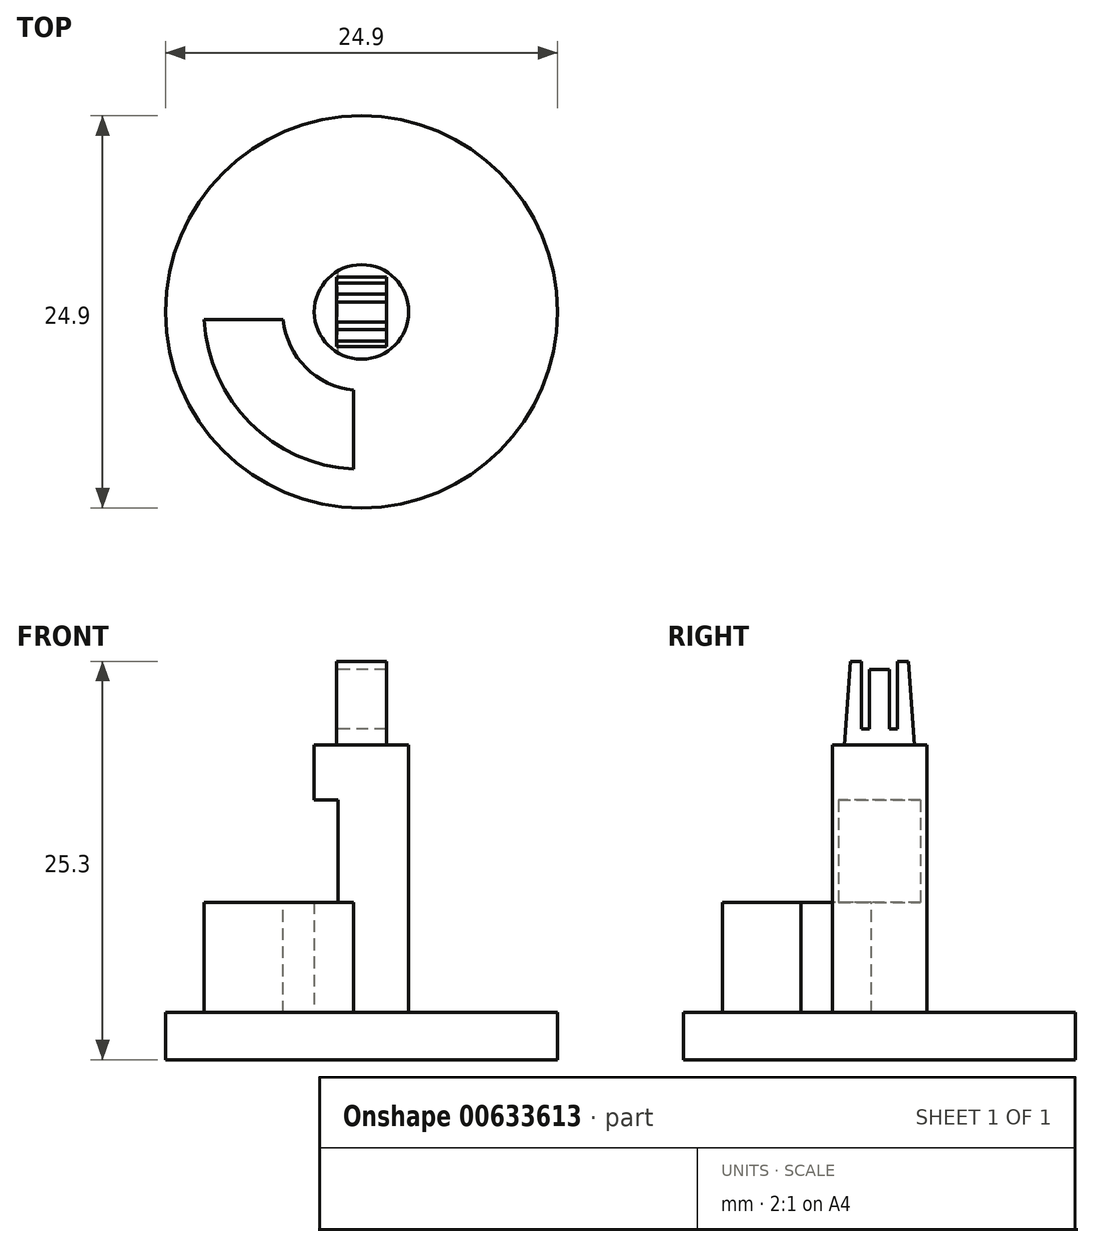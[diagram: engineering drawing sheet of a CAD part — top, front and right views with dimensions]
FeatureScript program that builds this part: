
annotation { "Feature Type Name" : "Feature", "Feature Type Description" : "" }
export const myFeature = defineFeature(function(context is Context, id is Id, definition is map)
    precondition{}
    {
        {
            var Q0;
            Q0=qCreatedBy(makeId("Top.planeOp"),FACE);
            var sketch = newSketch(context, id + "F0", { "sketchPlane" : qUnion([Q0])});
            skCircle(sketch, "E0", {"center": v(0, 0) * mm, "radius": 12.45 * mm});
            skSolve(sketch);
        }
        {
            var Q0;
            Q0=makeQuery(id+"F0.imprint","IMPRINT",FACE,{"disambiguationData":[TD([[makeQuery(id+"F0.imprint","IMPRINT",EDGE,{"derivedFrom":sQuery(id+"F0.wireOp",EDGE,"E0")}),1.0]])]});
            extrude(context, id + "F1", {"entities" : qUnion([Q0]), "depth" : 10 * mm, "offsetDistance" : 25 * mm});
        }
        {
            var Q0;
            Q0=makeQuery(id+"F1.opExtrude","CAP_FACE",FACE,{"disambiguationData":[OSD([sQuery(id+"F0.wireOp",EDGE,"E0")])],"isStart":false});
            var sketch = newSketch(context, id + "F2", { "sketchPlane" : qUnion([Q0])});
            skLineSegment(sketch, "E1", {"start": v(0, 12.45) * mm, "end": v(0, 0) * mm, "construction": true});
            skLineSegment(sketch, "E2", {"start": v(12.45, 0) * mm, "end": v(0, 0) * mm, "construction": true});
            skLineSegment(sketch, "E3", {"start": v(0, -12.45) * mm, "end": v(0, 0) * mm, "construction": true});
            skLineSegment(sketch, "E4", {"start": v(-12.45, 0) * mm, "end": v(0, 0) * mm, "construction": true});
            skCircle(sketch, "E5", {"center": v(0, 0) * mm, "radius": 3 * mm});
            skPoint(sketch, "E6", {"position": v(9.99, 0.5) * mm});
            skPoint(sketch, "E7", {"position": v(0.5, 9.99) * mm});
            skPoint(sketch, "E8", {"position": v(0.5, 4.97) * mm});
            skPoint(sketch, "E9", {"position": v(4.97, 0.5) * mm});
            skArc(sketch, "E10", {"start": v(9.99, 0.5) * mm, "mid": v(7.07, 7.07) * mm, "end": v(0.5, 9.99) * mm});
            skArc(sketch, "E11", {"start": v(0.5, 4.97) * mm, "mid": v(3.54, 3.54) * mm, "end": v(4.97, 0.5) * mm});
            skLineSegment(sketch, "E12", {"start": v(0.5, 9.99) * mm, "end": v(0.5, 4.97) * mm});
            skLineSegment(sketch, "E13", {"start": v(9.99, 0.5) * mm, "end": v(4.97, 0.5) * mm});
            skLineSegment(sketch, "E14.MirrorCS", {"start": v(9.99, -0.5) * mm, "end": v(4.97, -0.5) * mm});
            skArc(sketch, "E15.MirrorCS", {"start": v(9.99, -0.5) * mm, "mid": v(7.07, -7.07) * mm, "end": v(0.5, -9.99) * mm});
            skArc(sketch, "E16.MirrorCS", {"start": v(0.5, -4.97) * mm, "mid": v(3.54, -3.54) * mm, "end": v(4.97, -0.5) * mm});
            skLineSegment(sketch, "E17.MirrorCS", {"start": v(0.5, -9.99) * mm, "end": v(0.5, -4.97) * mm});
            skArc(sketch, "E18.MirrorCS", {"start": v(-0.5, -4.97) * mm, "mid": v(-3.54, -3.54) * mm, "end": v(-4.97, -0.5) * mm});
            skLineSegment(sketch, "E19.MirrorCS", {"start": v(-0.5, -9.99) * mm, "end": v(-0.5, -4.97) * mm});
            skArc(sketch, "E20.MirrorCS", {"start": v(-9.99, -0.5) * mm, "mid": v(-7.07, -7.07) * mm, "end": v(-0.5, -9.99) * mm});
            skLineSegment(sketch, "E21.MirrorCS", {"start": v(-9.99, -0.5) * mm, "end": v(-4.97, -0.5) * mm});
            skArc(sketch, "E22.MirrorCS", {"start": v(-0.5, 4.97) * mm, "mid": v(-3.54, 3.54) * mm, "end": v(-4.97, 0.5) * mm});
            skLineSegment(sketch, "E23.MirrorCS", {"start": v(-0.5, 9.99) * mm, "end": v(-0.5, 4.97) * mm});
            skArc(sketch, "E24.MirrorCS", {"start": v(-9.99, 0.5) * mm, "mid": v(-7.07, 7.07) * mm, "end": v(-0.5, 9.99) * mm});
            skLineSegment(sketch, "E25.MirrorCS", {"start": v(-9.99, 0.5) * mm, "end": v(-4.97, 0.5) * mm});
            skSolve(sketch);
        }
        {
            var Q0;
            Q0=makeQuery(id+"F2.imprint","IMPRINT",FACE,{"disambiguationData":[TD([[makeQuery(id+"F2.imprint","IMPRINT",EDGE,{"derivedFrom":sQuery(id+"F2.wireOp",EDGE,"E5")}),1.0]])]});
            extrude(context, id + "F3", {"entities" : qUnion([Q0]), "operationType" : NewBodyOperationType.ADD, "depth" : 10 * mm, "offsetDistance" : 25 * mm});
        }
        {
            var Q0;
            Q0=makeQuery(id+"F1.opExtrude","CAP_FACE",FACE,{"disambiguationData":[OSD([sQuery(id+"F0.wireOp",EDGE,"E0")])],"isStart":false});
            var sketch = newSketch(context, id + "F4", { "sketchPlane" : qUnion([Q0])});
            skLineSegment(sketch, "E26.bottom", {"start": v(-4.5, -3) * mm, "end": v(-1.5, -3) * mm});
            skLineSegment(sketch, "E26.top", {"start": v(-4.5, 3) * mm, "end": v(-1.5, 3) * mm});
            skLineSegment(sketch, "E26.left", {"start": v(-4.5, -3) * mm, "end": v(-4.5, 3) * mm});
            skLineSegment(sketch, "E26.right", {"start": v(-1.5, -3) * mm, "end": v(-1.5, 3) * mm});
            skPoint(sketch, "E26.middle", {"position": v(-3, 0) * mm});
            skSolve(sketch);
        }
        {
            var Q0;
            Q0 = qSketchRegion(id + "F4", true);
            extrude(context, id + "F5", {"entities" : qUnion([Q0]), "operationType" : NewBodyOperationType.REMOVE, "depth" : 6.5 * mm, "offsetDistance" : 25 * mm});
        }
        {
            var Q0;
            Q0=makeQuery(id+"F3.opExtrude","CAP_FACE",FACE,{"disambiguationData":[OSD([sQuery(id+"F2.wireOp",EDGE,"E5")])],"isStart":false});
            var sketch = newSketch(context, id + "F6", { "sketchPlane" : qUnion([Q0])});
            skLineSegment(sketch, "E27.bottom", {"start": v(1.58, -2.22) * mm, "end": v(-1.58, -2.22) * mm});
            skLineSegment(sketch, "E27.top", {"start": v(1.58, 2.21) * mm, "end": v(-1.58, 2.21) * mm});
            skLineSegment(sketch, "E27.left", {"start": v(1.58, -2.21) * mm, "end": v(1.58, 2.22) * mm});
            skLineSegment(sketch, "E27.right", {"start": v(-1.58, -2.22) * mm, "end": v(-1.58, 2.21) * mm});
            skPoint(sketch, "E27.middle", {"position": v(0, 0) * mm});
            skSolve(sketch);
        }
        {
            var Q0;
            Q0=makeQuery(id+"F6.imprint","IMPRINT",FACE,{"disambiguationData":[TD([[makeQuery(id+"F6.imprint","IMPRINT",EDGE,{"derivedFrom":sQuery(id+"F6.wireOp",EDGE,"E27.bottom")}),-1.0]])]});
            extrude(context, id + "F7", {"entities" : qUnion([Q0]), "operationType" : NewBodyOperationType.ADD, "depth" : 5.3 * mm, "offsetDistance" : 25 * mm});
        }
        {
            var Q0;
            Q0=makeQuery(id+"F7.opExtrude","CAP_FACE",FACE,{"disambiguationData":[OSD([sQuery(id+"F6.wireOp",EDGE,"E27.bottom"),sQuery(id+"F6.wireOp",EDGE,"E27.top"),sQuery(id+"F6.wireOp",EDGE,"E27.left"),sQuery(id+"F6.wireOp",EDGE,"E27.right")])],"isStart":false});
            var sketch = newSketch(context, id + "F8", { "sketchPlane" : qUnion([Q0])});
            skLineSegment(sketch, "E28.bottom", {"start": v(1.58, -1.14) * mm, "end": v(-1.58, -1.14) * mm});
            skLineSegment(sketch, "E28.top", {"start": v(1.58, 1.14) * mm, "end": v(-1.58, 1.14) * mm});
            skLineSegment(sketch, "E28.left", {"start": v(1.58, -1.14) * mm, "end": v(1.58, 1.14) * mm});
            skLineSegment(sketch, "E28.right", {"start": v(-1.58, -1.14) * mm, "end": v(-1.58, 1.14) * mm});
            skPoint(sketch, "E28.middle", {"position": v(0, 0) * mm});
            skLineSegment(sketch, "E29.top", {"start": v(1.58, 0.63) * mm, "end": v(-1.58, 0.63) * mm});
            skLineSegment(sketch, "E29.left", {"start": v(1.58, 1.14) * mm, "end": v(1.58, 0.63) * mm});
            skLineSegment(sketch, "E29.right", {"start": v(-1.58, 1.14) * mm, "end": v(-1.58, 0.63) * mm});
            skLineSegment(sketch, "E30", {"start": v(1.58, 0) * mm, "end": v(-1.58, 0) * mm, "construction": true});
            skLineSegment(sketch, "E31.MirrorCS", {"start": v(1.58, -0.63) * mm, "end": v(-1.58, -0.63) * mm});
            skSolve(sketch);
        }
        {
            var Q0;
            Q0=makeQuery(id+"F8.imprint","IMPRINT",FACE,{"disambiguationData":[TD([[makeQuery(id+"F8.imprint","IMPRINT",EDGE,{"derivedFrom":sQuery(id+"F8.wireOp",EDGE,"E28.top")}),1.0]])]});
            var Q1;
            {var subQ0=sQuery(id+"F8.wireOp",EDGE,"E28.bottom");Q1=makeQuery(id+"F8.imprint","IMPRINT",FACE,{"disambiguationData":[TD([[makeQuery(id+"F8.imprint","IMPRINT",EDGE,{"derivedFrom":subQ0}),-1.0]])]});}
            extrude(context, id + "F9", {"entities" : qUnion([Q0, Q1]), "operationType" : NewBodyOperationType.REMOVE, "oppositeDirection" : true, "depth" : 4.3 * mm, "offsetDistance" : 25 * mm});
        }
        {
            var Q0;
            Q0=makeQuery(id+"F7.opExtrude","SWEPT_FACE",FACE,{"disambiguationData":[OSD([sQuery(id+"F6.wireOp",EDGE,"E27.right")])]});
            var sketch = newSketch(context, id + "F10", { "sketchPlane" : qUnion([Q0])});
            skLineSegment(sketch, "E32", {"start": v(0, 33.13) * mm, "end": v(0, 21.21) * mm, "construction": true});
            skPoint(sketch, "E32.startSnap0", {"position": v(0, 25.3) * mm});
            skPoint(sketch, "E32.endSnap0", {"position": v(0, 20) * mm});
            skPoint(sketch, "E33", {"position": v(-1.84, 25.3) * mm});
            skLineSegment(sketch, "E34", {"start": v(-1.84, 25.3) * mm, "end": v(-2.22, 20) * mm});
            skLineSegment(sketch, "E35.MirrorCS", {"start": v(1.84, 25.3) * mm, "end": v(2.22, 20) * mm});
            skSolve(sketch);
        }
        {
            var Q0;
            {var subQ0=sQuery(id+"F10.wireOp",EDGE,"E34");Q0=makeQuery(id+"F10.imprint","IMPRINT",FACE,{"disambiguationData":[TD([[makeQuery(id+"F10.imprint","IMPRINT",EDGE,{"derivedFrom":subQ0}),-1.0]])]});}
            var Q1;
            {var subQ0=sQuery(id+"F10.wireOp",EDGE,"E35.MirrorCS");Q1=makeQuery(id+"F10.imprint","IMPRINT",FACE,{"disambiguationData":[TD([[makeQuery(id+"F10.imprint","IMPRINT",EDGE,{"derivedFrom":subQ0}),1.0]])]});}
            extrude(context, id + "F11", {"entities" : qUnion([Q0, Q1]), "operationType" : NewBodyOperationType.REMOVE, "endBound" : BoundingType.THROUGH_ALL, "oppositeDirection" : true, "depth" : 25 * mm, "offsetDistance" : 25 * mm});
        }
        {
            var Q0;
            Q0=makeQuery(id+"F7.opExtrude","SWEPT_FACE",FACE,{"disambiguationData":[OSD([sQuery(id+"F6.wireOp",EDGE,"E27.right")])]});
            var sketch = newSketch(context, id + "F12", { "sketchPlane" : qUnion([Q0])});
            skLineSegment(sketch, "E36.bottom", {"start": v(-0.63, 25.3) * mm, "end": v(0.63, 25.3) * mm});
            skLineSegment(sketch, "E36.top", {"start": v(-0.63, 24.8) * mm, "end": v(0.63, 24.8) * mm});
            skLineSegment(sketch, "E36.left", {"start": v(-0.63, 25.3) * mm, "end": v(-0.63, 24.8) * mm});
            skLineSegment(sketch, "E36.right", {"start": v(0.63, 25.3) * mm, "end": v(0.63, 24.8) * mm});
            skSolve(sketch);
        }
        {
            var Q0;
            Q0 = qSketchRegion(id + "F12", true);
            extrude(context, id + "F13", {"entities" : qUnion([Q0]), "operationType" : NewBodyOperationType.REMOVE, "endBound" : BoundingType.THROUGH_ALL, "oppositeDirection" : true, "depth" : 25 * mm, "offsetDistance" : 25 * mm});
        }
        {
            var Q0;
            Q0=makeQuery(id+"F2.imprint","IMPRINT",FACE,{"disambiguationData":[TD([[makeQuery(id+"F2.imprint","IMPRINT",EDGE,{"derivedFrom":sQuery(id+"F2.wireOp",EDGE,"E10")}),1.0]])]});
            var Q1;
            Q1=makeQuery(id+"F2.imprint","IMPRINT",FACE,{"disambiguationData":[TD([[makeQuery(id+"F2.imprint","IMPRINT",EDGE,{"derivedFrom":sQuery(id+"F2.wireOp",EDGE,"E14.MirrorCS")}),1.0]])]});
            var Q2;
            Q2=makeQuery(id+"F2.imprint","IMPRINT",FACE,{"disambiguationData":[TD([[makeQuery(id+"F2.imprint","IMPRINT",EDGE,{"derivedFrom":sQuery(id+"F2.wireOp",EDGE,"E18.MirrorCS")}),1.0]])]});
            var Q3;
            Q3=makeQuery(id+"F2.imprint","IMPRINT",FACE,{"disambiguationData":[TD([[makeQuery(id+"F2.imprint","IMPRINT",EDGE,{"derivedFrom":sQuery(id+"F2.wireOp",EDGE,"E22.MirrorCS")}),-1.0]])]});
            extrude(context, id + "F14", {"entities" : qUnion([Q0, Q1, Q2, Q3]), "operationType" : NewBodyOperationType.REMOVE, "oppositeDirection" : true, "depth" : 7 * mm, "offsetDistance" : 25 * mm});
        }
    });
